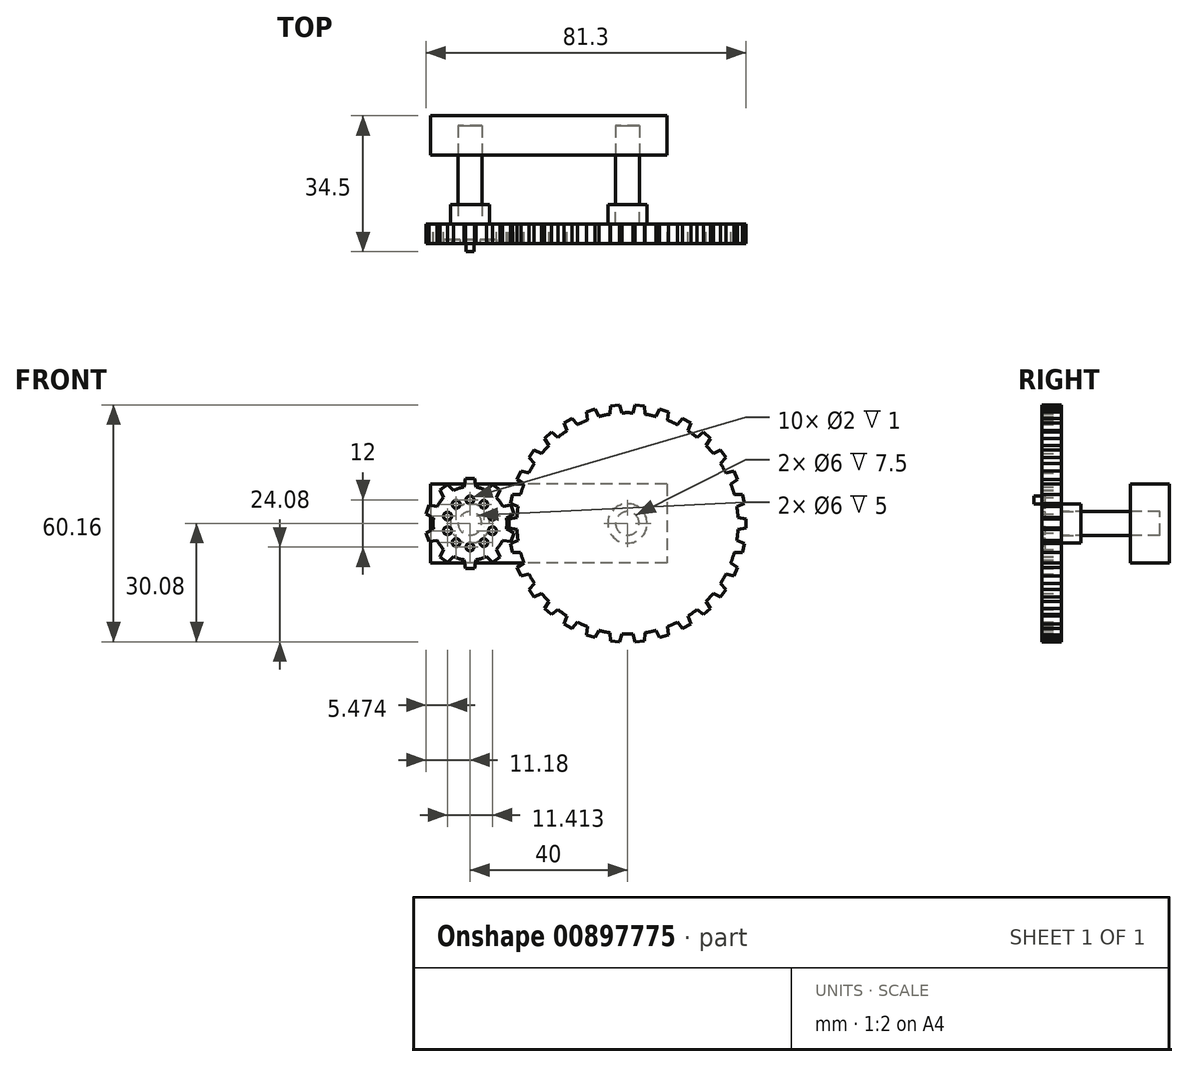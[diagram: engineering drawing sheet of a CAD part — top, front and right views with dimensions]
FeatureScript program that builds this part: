
annotation { "Feature Type Name" : "Feature", "Feature Type Description" : "" }
export const myFeature = defineFeature(function(context is Context, id is Id, definition is map)
    precondition{}
    {
        {
            var Q0;
            Q0=qCreatedBy(makeId("Front.planeOp"),FACE);
            var sketch = newSketch(context, id + "F0", { "sketchPlane" : qUnion([Q0])});
            skCircle(sketch, "E0", {"center": v(0, 0) * mm, "radius": 3 * mm});
            skCircle(sketch, "E1", {"center": v(0, 0) * mm, "radius": 5 * mm});
            skCircle(sketch, "E2", {"center": v(40, 0) * mm, "radius": 3 * mm});
            skCircle(sketch, "E3", {"center": v(40, 0) * mm, "radius": 5 * mm});
            skSolve(sketch);
        }
        {
            var Q0;
            Q0 = qSketchRegion(id + "F0", true);
            extrude(context, id + "F1", {"entities" : qUnion([Q0]), "endBound" : BoundingType.SYMMETRIC, "depth" : 5 * mm, "offsetDistance" : 25 * mm});
        }
        {
            var Q0;
            Q0=makeQuery(id+"F1.opExtrude","CAP_FACE",FACE,{"disambiguationData":[OSD([sQuery(id+"F0.wireOp",EDGE,"E0"),sQuery(id+"F0.wireOp",EDGE,"E1")])],"isStart":false});
            var sketch = newSketch(context, id + "F2", { "sketchPlane" : qUnion([Q0])});
            skCircle(sketch, "E4", {"center": v(0, 0) * mm, "radius": 9.38 * mm});
            skLineSegment(sketch, "E5", {"start": v(0, 11.38) * mm, "end": v(1.18, 11.38) * mm});
            skLineSegment(sketch, "E6", {"start": v(1.18, 11.38) * mm, "end": v(1.55, 9.25) * mm});
            skLineSegment(sketch, "E7.MirrorCS", {"start": v(0, 11.38) * mm, "end": v(-1.18, 11.38) * mm});
            skLineSegment(sketch, "E8.MirrorCS", {"start": v(-1.18, 11.38) * mm, "end": v(-1.55, 9.25) * mm});
            skLineSegment(sketch, "E9.1.0", {"start": v(-7.64, 8.51) * mm, "end": v(-6.7, 6.57) * mm});
            skLineSegment(sketch, "E9.1.1", {"start": v(-6.69, 9.2) * mm, "end": v(-7.64, 8.51) * mm});
            skLineSegment(sketch, "E9.1.2", {"start": v(-6.69, 9.2) * mm, "end": v(-5.73, 9.9) * mm});
            skLineSegment(sketch, "E9.1.3", {"start": v(-5.73, 9.9) * mm, "end": v(-4.18, 8.4) * mm});
            skLineSegment(sketch, "E9.2.0", {"start": v(-11.18, 2.4) * mm, "end": v(-9.27, 1.38) * mm});
            skLineSegment(sketch, "E9.2.1", {"start": v(-10.82, 3.52) * mm, "end": v(-11.18, 2.4) * mm});
            skLineSegment(sketch, "E9.2.2", {"start": v(-10.82, 3.52) * mm, "end": v(-10.45, 4.64) * mm});
            skLineSegment(sketch, "E9.2.3", {"start": v(-10.45, 4.64) * mm, "end": v(-8.31, 4.33) * mm});
            skLineSegment(sketch, "E10.2.3.0", {"start": v(-10.45, -4.64) * mm, "end": v(-8.31, -4.33) * mm});
            skLineSegment(sketch, "E10.3.3.0", {"start": v(-10.82, -3.52) * mm, "end": v(-10.45, -4.64) * mm});
            skLineSegment(sketch, "E10.6.3.0", {"start": v(-10.82, -3.52) * mm, "end": v(-11.18, -2.4) * mm});
            skLineSegment(sketch, "E10.9.3.0", {"start": v(-11.18, -2.4) * mm, "end": v(-9.27, -1.38) * mm});
            skLineSegment(sketch, "E10.2.4.0", {"start": v(-5.73, -9.9) * mm, "end": v(-4.18, -8.4) * mm});
            skLineSegment(sketch, "E10.3.4.0", {"start": v(-6.69, -9.2) * mm, "end": v(-5.73, -9.9) * mm});
            skLineSegment(sketch, "E10.6.4.0", {"start": v(-6.69, -9.2) * mm, "end": v(-7.64, -8.51) * mm});
            skLineSegment(sketch, "E10.9.4.0", {"start": v(-7.64, -8.51) * mm, "end": v(-6.7, -6.57) * mm});
            skLineSegment(sketch, "E10.2.5.0", {"start": v(1.18, -11.38) * mm, "end": v(1.55, -9.25) * mm});
            skLineSegment(sketch, "E10.3.5.0", {"start": v(0, -11.38) * mm, "end": v(1.18, -11.38) * mm});
            skLineSegment(sketch, "E10.6.5.0", {"start": v(0, -11.38) * mm, "end": v(-1.18, -11.38) * mm});
            skLineSegment(sketch, "E10.9.5.0", {"start": v(-1.18, -11.38) * mm, "end": v(-1.55, -9.25) * mm});
            skLineSegment(sketch, "E10.2.6.0", {"start": v(7.64, -8.51) * mm, "end": v(6.7, -6.57) * mm});
            skLineSegment(sketch, "E10.3.6.0", {"start": v(6.69, -9.2) * mm, "end": v(7.64, -8.51) * mm});
            skLineSegment(sketch, "E10.6.6.0", {"start": v(6.69, -9.2) * mm, "end": v(5.73, -9.9) * mm});
            skLineSegment(sketch, "E10.9.6.0", {"start": v(5.73, -9.9) * mm, "end": v(4.18, -8.4) * mm});
            skLineSegment(sketch, "E10.2.7.0", {"start": v(11.18, -2.4) * mm, "end": v(9.27, -1.38) * mm});
            skLineSegment(sketch, "E10.3.7.0", {"start": v(10.82, -3.52) * mm, "end": v(11.18, -2.4) * mm});
            skLineSegment(sketch, "E10.6.7.0", {"start": v(10.82, -3.52) * mm, "end": v(10.45, -4.64) * mm});
            skLineSegment(sketch, "E10.9.7.0", {"start": v(10.45, -4.64) * mm, "end": v(8.31, -4.33) * mm});
            skLineSegment(sketch, "E10.2.8.0", {"start": v(10.45, 4.64) * mm, "end": v(8.31, 4.33) * mm});
            skLineSegment(sketch, "E10.3.8.0", {"start": v(10.82, 3.52) * mm, "end": v(10.45, 4.64) * mm});
            skLineSegment(sketch, "E10.6.8.0", {"start": v(10.82, 3.52) * mm, "end": v(11.18, 2.4) * mm});
            skLineSegment(sketch, "E10.9.8.0", {"start": v(11.18, 2.4) * mm, "end": v(9.27, 1.38) * mm});
            skLineSegment(sketch, "E10.2.9.0", {"start": v(5.73, 9.9) * mm, "end": v(4.18, 8.4) * mm});
            skLineSegment(sketch, "E10.3.9.0", {"start": v(6.69, 9.2) * mm, "end": v(5.73, 9.9) * mm});
            skLineSegment(sketch, "E10.6.9.0", {"start": v(6.69, 9.2) * mm, "end": v(7.64, 8.51) * mm});
            skLineSegment(sketch, "E10.9.9.0", {"start": v(7.64, 8.51) * mm, "end": v(6.7, 6.57) * mm});
            skSolve(sketch);
        }
        {
            var Q0;
            Q0 = qSketchRegion(id + "F2", true);
            extrude(context, id + "F3", {"entities" : qUnion([Q0]), "operationType" : NewBodyOperationType.ADD, "depth" : 5 * mm, "offsetDistance" : 25 * mm});
        }
        {
            var Q0;
            Q0=makeQuery(id+"F1.opExtrude","CAP_FACE",FACE,{"disambiguationData":[OSD([sQuery(id+"F0.wireOp",EDGE,"E2"),sQuery(id+"F0.wireOp",EDGE,"E3")])],"isStart":false});
            var sketch = newSketch(context, id + "F4", { "sketchPlane" : qUnion([Q0])});
            skCircle(sketch, "E11", {"center": v(40, 0) * mm, "radius": 28.13 * mm});
            skLineSegment(sketch, "E12", {"start": v(9.88, 0) * mm, "end": v(9.88, 1.18) * mm});
            skLineSegment(sketch, "E13", {"start": v(9.88, 1.18) * mm, "end": v(11.92, 1.54) * mm});
            skLineSegment(sketch, "E14.MirrorCS", {"start": v(9.88, 0) * mm, "end": v(9.88, -1.18) * mm});
            skLineSegment(sketch, "E15.MirrorCS", {"start": v(9.88, -1.18) * mm, "end": v(11.92, -1.54) * mm});
            skLineSegment(sketch, "E16.1.0", {"start": v(10.53, -6.26) * mm, "end": v(10.29, -5.11) * mm});
            skLineSegment(sketch, "E16.1.1", {"start": v(10.29, -5.11) * mm, "end": v(12.21, -4.33) * mm});
            skLineSegment(sketch, "E16.1.2", {"start": v(10.53, -6.26) * mm, "end": v(10.78, -7.42) * mm});
            skLineSegment(sketch, "E16.1.3", {"start": v(10.78, -7.42) * mm, "end": v(12.85, -7.34) * mm});
            skLineSegment(sketch, "E16.2.0", {"start": v(12.48, -12.25) * mm, "end": v(12, -11.18) * mm});
            skLineSegment(sketch, "E16.2.1", {"start": v(12, -11.18) * mm, "end": v(13.72, -10.02) * mm});
            skLineSegment(sketch, "E16.2.2", {"start": v(12.48, -12.25) * mm, "end": v(12.96, -13.33) * mm});
            skLineSegment(sketch, "E16.2.3", {"start": v(12.96, -13.33) * mm, "end": v(14.97, -12.83) * mm});
            skLineSegment(sketch, "E17.1.3.0", {"start": v(15.63, -17.7) * mm, "end": v(14.94, -16.75) * mm});
            skLineSegment(sketch, "E17.3.3.0", {"start": v(14.94, -16.75) * mm, "end": v(16.38, -15.26) * mm});
            skLineSegment(sketch, "E17.6.3.0", {"start": v(15.63, -17.7) * mm, "end": v(16.32, -18.66) * mm});
            skLineSegment(sketch, "E17.9.3.0", {"start": v(16.32, -18.66) * mm, "end": v(18.18, -17.75) * mm});
            skLineSegment(sketch, "E17.1.4.0", {"start": v(19.84, -22.39) * mm, "end": v(18.97, -21.6) * mm});
            skLineSegment(sketch, "E17.3.4.0", {"start": v(18.97, -21.6) * mm, "end": v(20.07, -19.84) * mm});
            skLineSegment(sketch, "E17.6.4.0", {"start": v(19.84, -22.39) * mm, "end": v(20.72, -23.18) * mm});
            skLineSegment(sketch, "E17.9.4.0", {"start": v(20.72, -23.18) * mm, "end": v(22.35, -21.9) * mm});
            skLineSegment(sketch, "E17.1.5.0", {"start": v(24.94, -26.09) * mm, "end": v(23.92, -25.5) * mm});
            skLineSegment(sketch, "E17.3.5.0", {"start": v(23.92, -25.5) * mm, "end": v(24.63, -23.55) * mm});
            skLineSegment(sketch, "E17.6.5.0", {"start": v(24.94, -26.09) * mm, "end": v(25.96, -26.68) * mm});
            skLineSegment(sketch, "E17.9.5.0", {"start": v(25.96, -26.68) * mm, "end": v(27.3, -25.09) * mm});
            skLineSegment(sketch, "E17.1.6.0", {"start": v(30.7, -28.65) * mm, "end": v(29.57, -28.29) * mm});
            skLineSegment(sketch, "E17.3.6.0", {"start": v(29.57, -28.29) * mm, "end": v(29.86, -26.23) * mm});
            skLineSegment(sketch, "E17.6.6.0", {"start": v(30.7, -28.65) * mm, "end": v(31.81, -29.01) * mm});
            skLineSegment(sketch, "E17.9.6.0", {"start": v(31.81, -29.01) * mm, "end": v(32.78, -27.18) * mm});
            skLineSegment(sketch, "E17.1.7.0", {"start": v(36.85, -29.96) * mm, "end": v(35.68, -29.84) * mm});
            skLineSegment(sketch, "E17.3.7.0", {"start": v(35.68, -29.84) * mm, "end": v(35.53, -27.77) * mm});
            skLineSegment(sketch, "E17.6.7.0", {"start": v(36.85, -29.96) * mm, "end": v(38.02, -30.08) * mm});
            skLineSegment(sketch, "E17.9.7.0", {"start": v(38.02, -30.08) * mm, "end": v(38.6, -28.09) * mm});
            skLineSegment(sketch, "E17.1.8.0", {"start": v(43.15, -29.96) * mm, "end": v(41.98, -30.08) * mm});
            skLineSegment(sketch, "E17.3.8.0", {"start": v(41.98, -30.08) * mm, "end": v(41.4, -28.09) * mm});
            skLineSegment(sketch, "E17.6.8.0", {"start": v(43.15, -29.96) * mm, "end": v(44.32, -29.84) * mm});
            skLineSegment(sketch, "E17.9.8.0", {"start": v(44.32, -29.84) * mm, "end": v(44.47, -27.77) * mm});
            skLineSegment(sketch, "E17.1.9.0", {"start": v(49.3, -28.65) * mm, "end": v(48.19, -29.01) * mm});
            skLineSegment(sketch, "E17.3.9.0", {"start": v(48.19, -29.01) * mm, "end": v(47.22, -27.18) * mm});
            skLineSegment(sketch, "E17.6.9.0", {"start": v(49.3, -28.65) * mm, "end": v(50.43, -28.29) * mm});
            skLineSegment(sketch, "E17.9.9.0", {"start": v(50.43, -28.29) * mm, "end": v(50.14, -26.23) * mm});
            skLineSegment(sketch, "E17.1.10.0", {"start": v(55.06, -26.09) * mm, "end": v(54.04, -26.68) * mm});
            skLineSegment(sketch, "E17.3.10.0", {"start": v(54.04, -26.68) * mm, "end": v(52.7, -25.09) * mm});
            skLineSegment(sketch, "E17.6.10.0", {"start": v(55.06, -26.09) * mm, "end": v(56.08, -25.5) * mm});
            skLineSegment(sketch, "E17.9.10.0", {"start": v(56.08, -25.5) * mm, "end": v(55.37, -23.55) * mm});
            skLineSegment(sketch, "E17.1.11.0", {"start": v(60.16, -22.39) * mm, "end": v(59.28, -23.18) * mm});
            skLineSegment(sketch, "E17.3.11.0", {"start": v(59.28, -23.18) * mm, "end": v(57.65, -21.9) * mm});
            skLineSegment(sketch, "E17.6.11.0", {"start": v(60.16, -22.39) * mm, "end": v(61.03, -21.6) * mm});
            skLineSegment(sketch, "E17.9.11.0", {"start": v(61.03, -21.6) * mm, "end": v(59.93, -19.84) * mm});
            skLineSegment(sketch, "E17.1.12.0", {"start": v(64.37, -17.7) * mm, "end": v(63.68, -18.66) * mm});
            skLineSegment(sketch, "E17.3.12.0", {"start": v(63.68, -18.66) * mm, "end": v(61.82, -17.75) * mm});
            skLineSegment(sketch, "E17.6.12.0", {"start": v(64.37, -17.7) * mm, "end": v(65.06, -16.75) * mm});
            skLineSegment(sketch, "E17.9.12.0", {"start": v(65.06, -16.75) * mm, "end": v(63.62, -15.26) * mm});
            skLineSegment(sketch, "E17.1.13.0", {"start": v(67.52, -12.25) * mm, "end": v(67.04, -13.33) * mm});
            skLineSegment(sketch, "E17.3.13.0", {"start": v(67.04, -13.33) * mm, "end": v(65.03, -12.83) * mm});
            skLineSegment(sketch, "E17.6.13.0", {"start": v(67.52, -12.25) * mm, "end": v(68, -11.18) * mm});
            skLineSegment(sketch, "E17.9.13.0", {"start": v(68, -11.18) * mm, "end": v(66.28, -10.02) * mm});
            skLineSegment(sketch, "E17.1.14.0", {"start": v(69.47, -6.26) * mm, "end": v(69.22, -7.42) * mm});
            skLineSegment(sketch, "E17.3.14.0", {"start": v(69.22, -7.42) * mm, "end": v(67.15, -7.34) * mm});
            skLineSegment(sketch, "E17.6.14.0", {"start": v(69.47, -6.26) * mm, "end": v(69.71, -5.11) * mm});
            skLineSegment(sketch, "E17.9.14.0", {"start": v(69.71, -5.11) * mm, "end": v(67.79, -4.33) * mm});
            skLineSegment(sketch, "E17.1.15.0", {"start": v(70.12, 0) * mm, "end": v(70.12, -1.18) * mm});
            skLineSegment(sketch, "E17.3.15.0", {"start": v(70.13, -1.18) * mm, "end": v(68.08, -1.54) * mm});
            skLineSegment(sketch, "E17.6.15.0", {"start": v(70.12, 0) * mm, "end": v(70.12, 1.18) * mm});
            skLineSegment(sketch, "E17.9.15.0", {"start": v(70.13, 1.18) * mm, "end": v(68.08, 1.54) * mm});
            skLineSegment(sketch, "E17.1.16.0", {"start": v(69.47, 6.26) * mm, "end": v(69.71, 5.11) * mm});
            skLineSegment(sketch, "E17.3.16.0", {"start": v(69.71, 5.11) * mm, "end": v(67.79, 4.33) * mm});
            skLineSegment(sketch, "E17.6.16.0", {"start": v(69.47, 6.26) * mm, "end": v(69.22, 7.42) * mm});
            skLineSegment(sketch, "E17.9.16.0", {"start": v(69.22, 7.42) * mm, "end": v(67.15, 7.34) * mm});
            skLineSegment(sketch, "E17.1.17.0", {"start": v(67.52, 12.25) * mm, "end": v(68, 11.18) * mm});
            skLineSegment(sketch, "E17.3.17.0", {"start": v(68, 11.18) * mm, "end": v(66.28, 10.02) * mm});
            skLineSegment(sketch, "E17.6.17.0", {"start": v(67.52, 12.25) * mm, "end": v(67.04, 13.33) * mm});
            skLineSegment(sketch, "E17.9.17.0", {"start": v(67.04, 13.33) * mm, "end": v(65.03, 12.83) * mm});
            skLineSegment(sketch, "E17.1.18.0", {"start": v(64.37, 17.7) * mm, "end": v(65.06, 16.75) * mm});
            skLineSegment(sketch, "E17.3.18.0", {"start": v(65.06, 16.75) * mm, "end": v(63.62, 15.26) * mm});
            skLineSegment(sketch, "E17.6.18.0", {"start": v(64.37, 17.7) * mm, "end": v(63.68, 18.66) * mm});
            skLineSegment(sketch, "E17.9.18.0", {"start": v(63.68, 18.66) * mm, "end": v(61.82, 17.75) * mm});
            skLineSegment(sketch, "E17.1.19.0", {"start": v(60.16, 22.39) * mm, "end": v(61.03, 21.6) * mm});
            skLineSegment(sketch, "E17.3.19.0", {"start": v(61.03, 21.6) * mm, "end": v(59.93, 19.84) * mm});
            skLineSegment(sketch, "E17.6.19.0", {"start": v(60.16, 22.39) * mm, "end": v(59.28, 23.18) * mm});
            skLineSegment(sketch, "E17.9.19.0", {"start": v(59.28, 23.18) * mm, "end": v(57.65, 21.9) * mm});
            skLineSegment(sketch, "E17.1.20.0", {"start": v(55.06, 26.09) * mm, "end": v(56.08, 25.5) * mm});
            skLineSegment(sketch, "E17.3.20.0", {"start": v(56.08, 25.5) * mm, "end": v(55.37, 23.55) * mm});
            skLineSegment(sketch, "E17.6.20.0", {"start": v(55.06, 26.09) * mm, "end": v(54.04, 26.68) * mm});
            skLineSegment(sketch, "E17.9.20.0", {"start": v(54.04, 26.68) * mm, "end": v(52.7, 25.09) * mm});
            skLineSegment(sketch, "E17.1.21.0", {"start": v(49.3, 28.65) * mm, "end": v(50.43, 28.29) * mm});
            skLineSegment(sketch, "E17.3.21.0", {"start": v(50.43, 28.29) * mm, "end": v(50.14, 26.23) * mm});
            skLineSegment(sketch, "E17.6.21.0", {"start": v(49.3, 28.65) * mm, "end": v(48.19, 29.01) * mm});
            skLineSegment(sketch, "E17.9.21.0", {"start": v(48.19, 29.01) * mm, "end": v(47.22, 27.18) * mm});
            skLineSegment(sketch, "E17.1.22.0", {"start": v(43.15, 29.96) * mm, "end": v(44.32, 29.84) * mm});
            skLineSegment(sketch, "E17.3.22.0", {"start": v(44.32, 29.84) * mm, "end": v(44.47, 27.77) * mm});
            skLineSegment(sketch, "E17.6.22.0", {"start": v(43.15, 29.96) * mm, "end": v(41.98, 30.08) * mm});
            skLineSegment(sketch, "E17.9.22.0", {"start": v(41.98, 30.08) * mm, "end": v(41.4, 28.09) * mm});
            skLineSegment(sketch, "E17.1.23.0", {"start": v(36.85, 29.96) * mm, "end": v(38.02, 30.08) * mm});
            skLineSegment(sketch, "E17.3.23.0", {"start": v(38.02, 30.08) * mm, "end": v(38.6, 28.09) * mm});
            skLineSegment(sketch, "E17.6.23.0", {"start": v(36.85, 29.96) * mm, "end": v(35.68, 29.84) * mm});
            skLineSegment(sketch, "E17.9.23.0", {"start": v(35.68, 29.84) * mm, "end": v(35.53, 27.77) * mm});
            skLineSegment(sketch, "E17.1.24.0", {"start": v(30.7, 28.65) * mm, "end": v(31.81, 29.01) * mm});
            skLineSegment(sketch, "E17.3.24.0", {"start": v(31.81, 29.01) * mm, "end": v(32.78, 27.18) * mm});
            skLineSegment(sketch, "E17.6.24.0", {"start": v(30.7, 28.65) * mm, "end": v(29.57, 28.29) * mm});
            skLineSegment(sketch, "E17.9.24.0", {"start": v(29.57, 28.29) * mm, "end": v(29.86, 26.23) * mm});
            skLineSegment(sketch, "E17.1.25.0", {"start": v(24.94, 26.09) * mm, "end": v(25.96, 26.68) * mm});
            skLineSegment(sketch, "E17.3.25.0", {"start": v(25.96, 26.68) * mm, "end": v(27.3, 25.09) * mm});
            skLineSegment(sketch, "E17.6.25.0", {"start": v(24.94, 26.09) * mm, "end": v(23.92, 25.5) * mm});
            skLineSegment(sketch, "E17.9.25.0", {"start": v(23.92, 25.5) * mm, "end": v(24.63, 23.55) * mm});
            skLineSegment(sketch, "E17.1.26.0", {"start": v(19.84, 22.39) * mm, "end": v(20.72, 23.18) * mm});
            skLineSegment(sketch, "E17.3.26.0", {"start": v(20.72, 23.18) * mm, "end": v(22.35, 21.9) * mm});
            skLineSegment(sketch, "E17.6.26.0", {"start": v(19.84, 22.39) * mm, "end": v(18.97, 21.6) * mm});
            skLineSegment(sketch, "E17.9.26.0", {"start": v(18.97, 21.6) * mm, "end": v(20.07, 19.84) * mm});
            skLineSegment(sketch, "E17.1.27.0", {"start": v(15.63, 17.7) * mm, "end": v(16.32, 18.66) * mm});
            skLineSegment(sketch, "E17.3.27.0", {"start": v(16.32, 18.66) * mm, "end": v(18.18, 17.75) * mm});
            skLineSegment(sketch, "E17.6.27.0", {"start": v(15.63, 17.7) * mm, "end": v(14.94, 16.75) * mm});
            skLineSegment(sketch, "E17.9.27.0", {"start": v(14.94, 16.75) * mm, "end": v(16.38, 15.26) * mm});
            skLineSegment(sketch, "E17.1.28.0", {"start": v(12.48, 12.25) * mm, "end": v(12.96, 13.33) * mm});
            skLineSegment(sketch, "E17.3.28.0", {"start": v(12.96, 13.33) * mm, "end": v(14.97, 12.83) * mm});
            skLineSegment(sketch, "E17.6.28.0", {"start": v(12.48, 12.25) * mm, "end": v(12, 11.18) * mm});
            skLineSegment(sketch, "E17.9.28.0", {"start": v(12, 11.18) * mm, "end": v(13.72, 10.02) * mm});
            skLineSegment(sketch, "E17.1.29.0", {"start": v(10.53, 6.26) * mm, "end": v(10.78, 7.42) * mm});
            skLineSegment(sketch, "E17.3.29.0", {"start": v(10.78, 7.42) * mm, "end": v(12.85, 7.34) * mm});
            skLineSegment(sketch, "E17.6.29.0", {"start": v(10.53, 6.26) * mm, "end": v(10.29, 5.11) * mm});
            skLineSegment(sketch, "E17.9.29.0", {"start": v(10.29, 5.11) * mm, "end": v(12.21, 4.33) * mm});
            skSolve(sketch);
        }
        {
            var Q0;
            Q0 = qSketchRegion(id + "F4", true);
            extrude(context, id + "F5", {"entities" : qUnion([Q0]), "operationType" : NewBodyOperationType.ADD, "depth" : 5 * mm, "offsetDistance" : 25 * mm});
        }
        {
            var Q0;
            Q0=makeQuery(id+"F3.opExtrude","CAP_FACE",FACE,{"disambiguationData":[OSD([sQuery(id+"F2.wireOp",EDGE,"E4"),sQuery(id+"F2.wireOp",EDGE,"E5"),sQuery(id+"F2.wireOp",EDGE,"E6"),sQuery(id+"F2.wireOp",EDGE,"E7.MirrorCS"),sQuery(id+"F2.wireOp",EDGE,"E8.MirrorCS"),sQuery(id+"F2.wireOp",EDGE,"E9.1.0"),sQuery(id+"F2.wireOp",EDGE,"E9.1.1"),sQuery(id+"F2.wireOp",EDGE,"E9.1.2"),sQuery(id+"F2.wireOp",EDGE,"E9.1.3"),sQuery(id+"F2.wireOp",EDGE,"E9.2.0"),sQuery(id+"F2.wireOp",EDGE,"E9.2.1"),sQuery(id+"F2.wireOp",EDGE,"E9.2.2"),sQuery(id+"F2.wireOp",EDGE,"E9.2.3"),sQuery(id+"F2.wireOp",EDGE,"E10.2.3.0"),sQuery(id+"F2.wireOp",EDGE,"E10.3.3.0"),sQuery(id+"F2.wireOp",EDGE,"E10.6.3.0"),sQuery(id+"F2.wireOp",EDGE,"E10.9.3.0"),sQuery(id+"F2.wireOp",EDGE,"E10.2.4.0"),sQuery(id+"F2.wireOp",EDGE,"E10.3.4.0"),sQuery(id+"F2.wireOp",EDGE,"E10.6.4.0"),sQuery(id+"F2.wireOp",EDGE,"E10.9.4.0"),sQuery(id+"F2.wireOp",EDGE,"E10.2.5.0"),sQuery(id+"F2.wireOp",EDGE,"E10.3.5.0"),sQuery(id+"F2.wireOp",EDGE,"E10.6.5.0"),sQuery(id+"F2.wireOp",EDGE,"E10.9.5.0"),sQuery(id+"F2.wireOp",EDGE,"E10.2.6.0"),sQuery(id+"F2.wireOp",EDGE,"E10.3.6.0"),sQuery(id+"F2.wireOp",EDGE,"E10.6.6.0"),sQuery(id+"F2.wireOp",EDGE,"E10.9.6.0"),sQuery(id+"F2.wireOp",EDGE,"E10.2.7.0"),sQuery(id+"F2.wireOp",EDGE,"E10.3.7.0"),sQuery(id+"F2.wireOp",EDGE,"E10.6.7.0"),sQuery(id+"F2.wireOp",EDGE,"E10.9.7.0"),sQuery(id+"F2.wireOp",EDGE,"E10.2.8.0"),sQuery(id+"F2.wireOp",EDGE,"E10.3.8.0"),sQuery(id+"F2.wireOp",EDGE,"E10.6.8.0"),sQuery(id+"F2.wireOp",EDGE,"E10.9.8.0"),sQuery(id+"F2.wireOp",EDGE,"E10.2.9.0"),sQuery(id+"F2.wireOp",EDGE,"E10.3.9.0"),sQuery(id+"F2.wireOp",EDGE,"E10.6.9.0"),sQuery(id+"F2.wireOp",EDGE,"E10.9.9.0")])],"isStart":false});
            var sketch = newSketch(context, id + "F6", { "sketchPlane" : qUnion([Q0])});
            skCircle(sketch, "E18", {"center": v(0, 6) * mm, "radius": 1 * mm});
            skCircle(sketch, "E19.1.0", {"center": v(-3.53, 4.85) * mm, "radius": 1 * mm});
            skCircle(sketch, "E19.2.0", {"center": v(-5.7, 1.85) * mm, "radius": 1 * mm});
            skPoint(sketch, "E19.center", {"position": v(0, 0) * mm});
            skCircle(sketch, "E20.1.3.0", {"center": v(-5.7, -1.85) * mm, "radius": 1 * mm});
            skCircle(sketch, "E20.1.4.0", {"center": v(-3.53, -4.85) * mm, "radius": 1 * mm});
            skCircle(sketch, "E20.1.5.0", {"center": v(0, -6) * mm, "radius": 1 * mm});
            skCircle(sketch, "E20.1.6.0", {"center": v(3.53, -4.85) * mm, "radius": 1 * mm});
            skCircle(sketch, "E20.1.7.0", {"center": v(5.7, -1.85) * mm, "radius": 1 * mm});
            skCircle(sketch, "E20.1.8.0", {"center": v(5.7, 1.85) * mm, "radius": 1 * mm});
            skCircle(sketch, "E20.1.9.0", {"center": v(3.53, 4.85) * mm, "radius": 1 * mm});
            skSolve(sketch);
        }
        {
            var Q0;
            Q0 = qSketchRegion(id + "F6", true);
            extrude(context, id + "F7", {"entities" : qUnion([Q0]), "operationType" : NewBodyOperationType.REMOVE, "oppositeDirection" : true, "depth" : 1 * mm, "offsetDistance" : 25 * mm});
        }
        {
            var Q0;
            Q0=makeQuery(id+"F3.opExtrude","CAP_FACE",FACE,{"disambiguationData":[OSD([sQuery(id+"F2.wireOp",EDGE,"E4"),sQuery(id+"F2.wireOp",EDGE,"E5"),sQuery(id+"F2.wireOp",EDGE,"E6"),sQuery(id+"F2.wireOp",EDGE,"E7.MirrorCS"),sQuery(id+"F2.wireOp",EDGE,"E8.MirrorCS"),sQuery(id+"F2.wireOp",EDGE,"E9.1.0"),sQuery(id+"F2.wireOp",EDGE,"E9.1.1"),sQuery(id+"F2.wireOp",EDGE,"E9.1.2"),sQuery(id+"F2.wireOp",EDGE,"E9.1.3"),sQuery(id+"F2.wireOp",EDGE,"E9.2.0"),sQuery(id+"F2.wireOp",EDGE,"E9.2.1"),sQuery(id+"F2.wireOp",EDGE,"E9.2.2"),sQuery(id+"F2.wireOp",EDGE,"E9.2.3"),sQuery(id+"F2.wireOp",EDGE,"E10.2.3.0"),sQuery(id+"F2.wireOp",EDGE,"E10.3.3.0"),sQuery(id+"F2.wireOp",EDGE,"E10.6.3.0"),sQuery(id+"F2.wireOp",EDGE,"E10.9.3.0"),sQuery(id+"F2.wireOp",EDGE,"E10.2.4.0"),sQuery(id+"F2.wireOp",EDGE,"E10.3.4.0"),sQuery(id+"F2.wireOp",EDGE,"E10.6.4.0"),sQuery(id+"F2.wireOp",EDGE,"E10.9.4.0"),sQuery(id+"F2.wireOp",EDGE,"E10.2.5.0"),sQuery(id+"F2.wireOp",EDGE,"E10.3.5.0"),sQuery(id+"F2.wireOp",EDGE,"E10.6.5.0"),sQuery(id+"F2.wireOp",EDGE,"E10.9.5.0"),sQuery(id+"F2.wireOp",EDGE,"E10.2.6.0"),sQuery(id+"F2.wireOp",EDGE,"E10.3.6.0"),sQuery(id+"F2.wireOp",EDGE,"E10.6.6.0"),sQuery(id+"F2.wireOp",EDGE,"E10.9.6.0"),sQuery(id+"F2.wireOp",EDGE,"E10.2.7.0"),sQuery(id+"F2.wireOp",EDGE,"E10.3.7.0"),sQuery(id+"F2.wireOp",EDGE,"E10.6.7.0"),sQuery(id+"F2.wireOp",EDGE,"E10.9.7.0"),sQuery(id+"F2.wireOp",EDGE,"E10.2.8.0"),sQuery(id+"F2.wireOp",EDGE,"E10.3.8.0"),sQuery(id+"F2.wireOp",EDGE,"E10.6.8.0"),sQuery(id+"F2.wireOp",EDGE,"E10.9.8.0"),sQuery(id+"F2.wireOp",EDGE,"E10.2.9.0"),sQuery(id+"F2.wireOp",EDGE,"E10.3.9.0"),sQuery(id+"F2.wireOp",EDGE,"E10.6.9.0"),sQuery(id+"F2.wireOp",EDGE,"E10.9.9.0")])],"isStart":false});
            var sketch = newSketch(context, id + "F8", { "sketchPlane" : qUnion([Q0])});
            skCircle(sketch, "E21", {"center": v(0, 6) * mm, "radius": 1 * mm});
            skSolve(sketch);
        }
        {
            var Q0;
            Q0 = qSketchRegion(id + "F8", true);
            extrude(context, id + "F9", {"entities" : qUnion([Q0]), "depth" : 2 * mm, "offsetDistance" : 25 * mm});
        }
        {
            var Q0;
            Q0=makeQuery(id+"F5.boolean.opBoolean","SPLIT",FACE,{"disambiguationData":[TD([makeQuery(id+"F1.opExtrude","SWEPT_FACE",FACE,{"disambiguationData":[OSD([sQuery(id+"F0.wireOp",EDGE,"E2")])]})])],"derivedFrom":makeQuery(id+"F5.opExtrude","CAP_FACE",FACE,{"disambiguationData":[OSD([sQuery(id+"F4.wireOp",EDGE,"E11"),sQuery(id+"F4.wireOp",EDGE,"E12"),sQuery(id+"F4.wireOp",EDGE,"E13"),sQuery(id+"F4.wireOp",EDGE,"E14.MirrorCS"),sQuery(id+"F4.wireOp",EDGE,"E15.MirrorCS"),sQuery(id+"F4.wireOp",EDGE,"E16.1.0"),sQuery(id+"F4.wireOp",EDGE,"E16.1.1"),sQuery(id+"F4.wireOp",EDGE,"E16.1.2"),sQuery(id+"F4.wireOp",EDGE,"E16.1.3"),sQuery(id+"F4.wireOp",EDGE,"E16.2.0"),sQuery(id+"F4.wireOp",EDGE,"E16.2.1"),sQuery(id+"F4.wireOp",EDGE,"E16.2.2"),sQuery(id+"F4.wireOp",EDGE,"E16.2.3"),sQuery(id+"F4.wireOp",EDGE,"E17.1.3.0"),sQuery(id+"F4.wireOp",EDGE,"E17.3.3.0"),sQuery(id+"F4.wireOp",EDGE,"E17.6.3.0"),sQuery(id+"F4.wireOp",EDGE,"E17.9.3.0"),sQuery(id+"F4.wireOp",EDGE,"E17.1.4.0"),sQuery(id+"F4.wireOp",EDGE,"E17.3.4.0"),sQuery(id+"F4.wireOp",EDGE,"E17.6.4.0"),sQuery(id+"F4.wireOp",EDGE,"E17.9.4.0"),sQuery(id+"F4.wireOp",EDGE,"E17.1.5.0"),sQuery(id+"F4.wireOp",EDGE,"E17.3.5.0"),sQuery(id+"F4.wireOp",EDGE,"E17.6.5.0"),sQuery(id+"F4.wireOp",EDGE,"E17.9.5.0"),sQuery(id+"F4.wireOp",EDGE,"E17.1.6.0"),sQuery(id+"F4.wireOp",EDGE,"E17.3.6.0"),sQuery(id+"F4.wireOp",EDGE,"E17.6.6.0"),sQuery(id+"F4.wireOp",EDGE,"E17.9.6.0"),sQuery(id+"F4.wireOp",EDGE,"E17.1.7.0"),sQuery(id+"F4.wireOp",EDGE,"E17.3.7.0"),sQuery(id+"F4.wireOp",EDGE,"E17.6.7.0"),sQuery(id+"F4.wireOp",EDGE,"E17.9.7.0"),sQuery(id+"F4.wireOp",EDGE,"E17.1.8.0"),sQuery(id+"F4.wireOp",EDGE,"E17.3.8.0"),sQuery(id+"F4.wireOp",EDGE,"E17.6.8.0"),sQuery(id+"F4.wireOp",EDGE,"E17.9.8.0"),sQuery(id+"F4.wireOp",EDGE,"E17.1.9.0"),sQuery(id+"F4.wireOp",EDGE,"E17.3.9.0"),sQuery(id+"F4.wireOp",EDGE,"E17.6.9.0"),sQuery(id+"F4.wireOp",EDGE,"E17.9.9.0"),sQuery(id+"F4.wireOp",EDGE,"E17.1.10.0"),sQuery(id+"F4.wireOp",EDGE,"E17.3.10.0"),sQuery(id+"F4.wireOp",EDGE,"E17.6.10.0"),sQuery(id+"F4.wireOp",EDGE,"E17.9.10.0"),sQuery(id+"F4.wireOp",EDGE,"E17.1.11.0"),sQuery(id+"F4.wireOp",EDGE,"E17.3.11.0"),sQuery(id+"F4.wireOp",EDGE,"E17.6.11.0"),sQuery(id+"F4.wireOp",EDGE,"E17.9.11.0"),sQuery(id+"F4.wireOp",EDGE,"E17.1.12.0"),sQuery(id+"F4.wireOp",EDGE,"E17.3.12.0"),sQuery(id+"F4.wireOp",EDGE,"E17.6.12.0"),sQuery(id+"F4.wireOp",EDGE,"E17.9.12.0"),sQuery(id+"F4.wireOp",EDGE,"E17.1.13.0"),sQuery(id+"F4.wireOp",EDGE,"E17.3.13.0"),sQuery(id+"F4.wireOp",EDGE,"E17.6.13.0"),sQuery(id+"F4.wireOp",EDGE,"E17.9.13.0"),sQuery(id+"F4.wireOp",EDGE,"E17.1.14.0"),sQuery(id+"F4.wireOp",EDGE,"E17.3.14.0"),sQuery(id+"F4.wireOp",EDGE,"E17.6.14.0"),sQuery(id+"F4.wireOp",EDGE,"E17.9.14.0"),sQuery(id+"F4.wireOp",EDGE,"E17.1.15.0"),sQuery(id+"F4.wireOp",EDGE,"E17.3.15.0"),sQuery(id+"F4.wireOp",EDGE,"E17.6.15.0"),sQuery(id+"F4.wireOp",EDGE,"E17.9.15.0"),sQuery(id+"F4.wireOp",EDGE,"E17.1.16.0"),sQuery(id+"F4.wireOp",EDGE,"E17.3.16.0"),sQuery(id+"F4.wireOp",EDGE,"E17.6.16.0"),sQuery(id+"F4.wireOp",EDGE,"E17.9.16.0"),sQuery(id+"F4.wireOp",EDGE,"E17.1.17.0"),sQuery(id+"F4.wireOp",EDGE,"E17.3.17.0"),sQuery(id+"F4.wireOp",EDGE,"E17.6.17.0"),sQuery(id+"F4.wireOp",EDGE,"E17.9.17.0"),sQuery(id+"F4.wireOp",EDGE,"E17.1.18.0"),sQuery(id+"F4.wireOp",EDGE,"E17.3.18.0"),sQuery(id+"F4.wireOp",EDGE,"E17.6.18.0"),sQuery(id+"F4.wireOp",EDGE,"E17.9.18.0"),sQuery(id+"F4.wireOp",EDGE,"E17.1.19.0"),sQuery(id+"F4.wireOp",EDGE,"E17.3.19.0"),sQuery(id+"F4.wireOp",EDGE,"E17.6.19.0"),sQuery(id+"F4.wireOp",EDGE,"E17.9.19.0"),sQuery(id+"F4.wireOp",EDGE,"E17.1.20.0"),sQuery(id+"F4.wireOp",EDGE,"E17.3.20.0"),sQuery(id+"F4.wireOp",EDGE,"E17.6.20.0"),sQuery(id+"F4.wireOp",EDGE,"E17.9.20.0"),sQuery(id+"F4.wireOp",EDGE,"E17.1.21.0"),sQuery(id+"F4.wireOp",EDGE,"E17.3.21.0"),sQuery(id+"F4.wireOp",EDGE,"E17.6.21.0"),sQuery(id+"F4.wireOp",EDGE,"E17.9.21.0"),sQuery(id+"F4.wireOp",EDGE,"E17.1.22.0"),sQuery(id+"F4.wireOp",EDGE,"E17.3.22.0"),sQuery(id+"F4.wireOp",EDGE,"E17.6.22.0"),sQuery(id+"F4.wireOp",EDGE,"E17.9.22.0"),sQuery(id+"F4.wireOp",EDGE,"E17.1.23.0"),sQuery(id+"F4.wireOp",EDGE,"E17.3.23.0"),sQuery(id+"F4.wireOp",EDGE,"E17.6.23.0"),sQuery(id+"F4.wireOp",EDGE,"E17.9.23.0"),sQuery(id+"F4.wireOp",EDGE,"E17.1.24.0"),sQuery(id+"F4.wireOp",EDGE,"E17.3.24.0"),sQuery(id+"F4.wireOp",EDGE,"E17.6.24.0"),sQuery(id+"F4.wireOp",EDGE,"E17.9.24.0"),sQuery(id+"F4.wireOp",EDGE,"E17.1.25.0"),sQuery(id+"F4.wireOp",EDGE,"E17.3.25.0"),sQuery(id+"F4.wireOp",EDGE,"E17.6.25.0"),sQuery(id+"F4.wireOp",EDGE,"E17.9.25.0"),sQuery(id+"F4.wireOp",EDGE,"E17.1.26.0"),sQuery(id+"F4.wireOp",EDGE,"E17.3.26.0"),sQuery(id+"F4.wireOp",EDGE,"E17.6.26.0"),sQuery(id+"F4.wireOp",EDGE,"E17.9.26.0"),sQuery(id+"F4.wireOp",EDGE,"E17.1.27.0"),sQuery(id+"F4.wireOp",EDGE,"E17.3.27.0"),sQuery(id+"F4.wireOp",EDGE,"E17.6.27.0"),sQuery(id+"F4.wireOp",EDGE,"E17.9.27.0"),sQuery(id+"F4.wireOp",EDGE,"E17.1.28.0"),sQuery(id+"F4.wireOp",EDGE,"E17.3.28.0"),sQuery(id+"F4.wireOp",EDGE,"E17.6.28.0"),sQuery(id+"F4.wireOp",EDGE,"E17.9.28.0"),sQuery(id+"F4.wireOp",EDGE,"E17.1.29.0"),sQuery(id+"F4.wireOp",EDGE,"E17.3.29.0"),sQuery(id+"F4.wireOp",EDGE,"E17.6.29.0"),sQuery(id+"F4.wireOp",EDGE,"E17.9.29.0")])],"isStart":true})});
            extrude(context, id + "F10", {"entities" : qUnion([Q0]), "depth" : 25 * mm, "offsetDistance" : 25 * mm});
        }
        {
            var Q0;
            Q0=makeQuery(id+"F3.boolean.opBoolean","SPLIT",FACE,{"disambiguationData":[TD([makeQuery(id+"F1.opExtrude","SWEPT_FACE",FACE,{"disambiguationData":[OSD([sQuery(id+"F0.wireOp",EDGE,"E0")])]})])],"derivedFrom":makeQuery(id+"F3.opExtrude","CAP_FACE",FACE,{"disambiguationData":[OSD([sQuery(id+"F2.wireOp",EDGE,"E4"),sQuery(id+"F2.wireOp",EDGE,"E5"),sQuery(id+"F2.wireOp",EDGE,"E6"),sQuery(id+"F2.wireOp",EDGE,"E7.MirrorCS"),sQuery(id+"F2.wireOp",EDGE,"E8.MirrorCS"),sQuery(id+"F2.wireOp",EDGE,"E9.1.0"),sQuery(id+"F2.wireOp",EDGE,"E9.1.1"),sQuery(id+"F2.wireOp",EDGE,"E9.1.2"),sQuery(id+"F2.wireOp",EDGE,"E9.1.3"),sQuery(id+"F2.wireOp",EDGE,"E9.2.0"),sQuery(id+"F2.wireOp",EDGE,"E9.2.1"),sQuery(id+"F2.wireOp",EDGE,"E9.2.2"),sQuery(id+"F2.wireOp",EDGE,"E9.2.3"),sQuery(id+"F2.wireOp",EDGE,"E10.2.3.0"),sQuery(id+"F2.wireOp",EDGE,"E10.3.3.0"),sQuery(id+"F2.wireOp",EDGE,"E10.6.3.0"),sQuery(id+"F2.wireOp",EDGE,"E10.9.3.0"),sQuery(id+"F2.wireOp",EDGE,"E10.2.4.0"),sQuery(id+"F2.wireOp",EDGE,"E10.3.4.0"),sQuery(id+"F2.wireOp",EDGE,"E10.6.4.0"),sQuery(id+"F2.wireOp",EDGE,"E10.9.4.0"),sQuery(id+"F2.wireOp",EDGE,"E10.2.5.0"),sQuery(id+"F2.wireOp",EDGE,"E10.3.5.0"),sQuery(id+"F2.wireOp",EDGE,"E10.6.5.0"),sQuery(id+"F2.wireOp",EDGE,"E10.9.5.0"),sQuery(id+"F2.wireOp",EDGE,"E10.2.6.0"),sQuery(id+"F2.wireOp",EDGE,"E10.3.6.0"),sQuery(id+"F2.wireOp",EDGE,"E10.6.6.0"),sQuery(id+"F2.wireOp",EDGE,"E10.9.6.0"),sQuery(id+"F2.wireOp",EDGE,"E10.2.7.0"),sQuery(id+"F2.wireOp",EDGE,"E10.3.7.0"),sQuery(id+"F2.wireOp",EDGE,"E10.6.7.0"),sQuery(id+"F2.wireOp",EDGE,"E10.9.7.0"),sQuery(id+"F2.wireOp",EDGE,"E10.2.8.0"),sQuery(id+"F2.wireOp",EDGE,"E10.3.8.0"),sQuery(id+"F2.wireOp",EDGE,"E10.6.8.0"),sQuery(id+"F2.wireOp",EDGE,"E10.9.8.0"),sQuery(id+"F2.wireOp",EDGE,"E10.2.9.0"),sQuery(id+"F2.wireOp",EDGE,"E10.3.9.0"),sQuery(id+"F2.wireOp",EDGE,"E10.6.9.0"),sQuery(id+"F2.wireOp",EDGE,"E10.9.9.0")])],"isStart":true})});
            extrude(context, id + "F11", {"entities" : qUnion([Q0]), "depth" : 25 * mm, "offsetDistance" : 25 * mm});
        }
        {
            var Q0;
            Q0=qCreatedBy(makeId("Front.planeOp"),FACE);
            cPlane(context, id + "F12", {"entities" : qUnion([Q0]), "cplaneType" : CPlaneType.OFFSET, "offset" : 25 * mm, "oppositeDirection" : true, "width" : 150 * mm, "height" : 150 * mm});
        }
        {
            var Q0;
            Q0=qCreatedBy(id+"F12.planeOp",FACE);
            var sketch = newSketch(context, id + "F13", { "sketchPlane" : qUnion([Q0])});
            skLineSegment(sketch, "E22.bottom", {"start": v(50, 10) * mm, "end": v(-10, 10) * mm});
            skLineSegment(sketch, "E22.top", {"start": v(50, -10) * mm, "end": v(-10, -10) * mm});
            skLineSegment(sketch, "E22.left", {"start": v(50, 10) * mm, "end": v(50, -10) * mm});
            skLineSegment(sketch, "E22.right", {"start": v(-10, 10) * mm, "end": v(-10, -10) * mm});
            skSolve(sketch);
        }
        {
            var Q0;
            Q0 = qSketchRegion(id + "F13", true);
            extrude(context, id + "F14", {"entities" : qUnion([Q0]), "depth" : 10 * mm, "offsetDistance" : 25 * mm});
        }
        {
            var Q0;
            Q0=makeQuery(id+"F10.opExtrude","SWEPT_BODY",BODY,{"disambiguationData":[OSD([sQuery(id+"F4.wireOp",EDGE,"E11"),sQuery(id+"F4.wireOp",EDGE,"E12"),sQuery(id+"F4.wireOp",EDGE,"E13"),sQuery(id+"F4.wireOp",EDGE,"E14.MirrorCS"),sQuery(id+"F4.wireOp",EDGE,"E15.MirrorCS"),sQuery(id+"F4.wireOp",EDGE,"E16.1.0"),sQuery(id+"F4.wireOp",EDGE,"E16.1.1"),sQuery(id+"F4.wireOp",EDGE,"E16.1.2"),sQuery(id+"F4.wireOp",EDGE,"E16.1.3"),sQuery(id+"F4.wireOp",EDGE,"E16.2.0"),sQuery(id+"F4.wireOp",EDGE,"E16.2.1"),sQuery(id+"F4.wireOp",EDGE,"E16.2.2"),sQuery(id+"F4.wireOp",EDGE,"E16.2.3"),sQuery(id+"F4.wireOp",EDGE,"E17.1.3.0"),sQuery(id+"F4.wireOp",EDGE,"E17.3.3.0"),sQuery(id+"F4.wireOp",EDGE,"E17.6.3.0"),sQuery(id+"F4.wireOp",EDGE,"E17.9.3.0"),sQuery(id+"F4.wireOp",EDGE,"E17.1.4.0"),sQuery(id+"F4.wireOp",EDGE,"E17.3.4.0"),sQuery(id+"F4.wireOp",EDGE,"E17.6.4.0"),sQuery(id+"F4.wireOp",EDGE,"E17.9.4.0"),sQuery(id+"F4.wireOp",EDGE,"E17.1.5.0"),sQuery(id+"F4.wireOp",EDGE,"E17.3.5.0"),sQuery(id+"F4.wireOp",EDGE,"E17.6.5.0"),sQuery(id+"F4.wireOp",EDGE,"E17.9.5.0"),sQuery(id+"F4.wireOp",EDGE,"E17.1.6.0"),sQuery(id+"F4.wireOp",EDGE,"E17.3.6.0"),sQuery(id+"F4.wireOp",EDGE,"E17.6.6.0"),sQuery(id+"F4.wireOp",EDGE,"E17.9.6.0"),sQuery(id+"F4.wireOp",EDGE,"E17.1.7.0"),sQuery(id+"F4.wireOp",EDGE,"E17.3.7.0"),sQuery(id+"F4.wireOp",EDGE,"E17.6.7.0"),sQuery(id+"F4.wireOp",EDGE,"E17.9.7.0"),sQuery(id+"F4.wireOp",EDGE,"E17.1.8.0"),sQuery(id+"F4.wireOp",EDGE,"E17.3.8.0"),sQuery(id+"F4.wireOp",EDGE,"E17.6.8.0"),sQuery(id+"F4.wireOp",EDGE,"E17.9.8.0"),sQuery(id+"F4.wireOp",EDGE,"E17.1.9.0"),sQuery(id+"F4.wireOp",EDGE,"E17.3.9.0"),sQuery(id+"F4.wireOp",EDGE,"E17.6.9.0"),sQuery(id+"F4.wireOp",EDGE,"E17.9.9.0"),sQuery(id+"F4.wireOp",EDGE,"E17.1.10.0"),sQuery(id+"F4.wireOp",EDGE,"E17.3.10.0"),sQuery(id+"F4.wireOp",EDGE,"E17.6.10.0"),sQuery(id+"F4.wireOp",EDGE,"E17.9.10.0"),sQuery(id+"F4.wireOp",EDGE,"E17.1.11.0"),sQuery(id+"F4.wireOp",EDGE,"E17.3.11.0"),sQuery(id+"F4.wireOp",EDGE,"E17.6.11.0"),sQuery(id+"F4.wireOp",EDGE,"E17.9.11.0"),sQuery(id+"F4.wireOp",EDGE,"E17.1.12.0"),sQuery(id+"F4.wireOp",EDGE,"E17.3.12.0"),sQuery(id+"F4.wireOp",EDGE,"E17.6.12.0"),sQuery(id+"F4.wireOp",EDGE,"E17.9.12.0"),sQuery(id+"F4.wireOp",EDGE,"E17.1.13.0"),sQuery(id+"F4.wireOp",EDGE,"E17.3.13.0"),sQuery(id+"F4.wireOp",EDGE,"E17.6.13.0"),sQuery(id+"F4.wireOp",EDGE,"E17.9.13.0"),sQuery(id+"F4.wireOp",EDGE,"E17.1.14.0"),sQuery(id+"F4.wireOp",EDGE,"E17.3.14.0"),sQuery(id+"F4.wireOp",EDGE,"E17.6.14.0"),sQuery(id+"F4.wireOp",EDGE,"E17.9.14.0"),sQuery(id+"F4.wireOp",EDGE,"E17.1.15.0"),sQuery(id+"F4.wireOp",EDGE,"E17.3.15.0"),sQuery(id+"F4.wireOp",EDGE,"E17.6.15.0"),sQuery(id+"F4.wireOp",EDGE,"E17.9.15.0"),sQuery(id+"F4.wireOp",EDGE,"E17.1.16.0"),sQuery(id+"F4.wireOp",EDGE,"E17.3.16.0"),sQuery(id+"F4.wireOp",EDGE,"E17.6.16.0"),sQuery(id+"F4.wireOp",EDGE,"E17.9.16.0"),sQuery(id+"F4.wireOp",EDGE,"E17.1.17.0"),sQuery(id+"F4.wireOp",EDGE,"E17.3.17.0"),sQuery(id+"F4.wireOp",EDGE,"E17.6.17.0"),sQuery(id+"F4.wireOp",EDGE,"E17.9.17.0"),sQuery(id+"F4.wireOp",EDGE,"E17.1.18.0"),sQuery(id+"F4.wireOp",EDGE,"E17.3.18.0"),sQuery(id+"F4.wireOp",EDGE,"E17.6.18.0"),sQuery(id+"F4.wireOp",EDGE,"E17.9.18.0"),sQuery(id+"F4.wireOp",EDGE,"E17.1.19.0"),sQuery(id+"F4.wireOp",EDGE,"E17.3.19.0"),sQuery(id+"F4.wireOp",EDGE,"E17.6.19.0"),sQuery(id+"F4.wireOp",EDGE,"E17.9.19.0"),sQuery(id+"F4.wireOp",EDGE,"E17.1.20.0"),sQuery(id+"F4.wireOp",EDGE,"E17.3.20.0"),sQuery(id+"F4.wireOp",EDGE,"E17.6.20.0"),sQuery(id+"F4.wireOp",EDGE,"E17.9.20.0"),sQuery(id+"F4.wireOp",EDGE,"E17.1.21.0"),sQuery(id+"F4.wireOp",EDGE,"E17.3.21.0"),sQuery(id+"F4.wireOp",EDGE,"E17.6.21.0"),sQuery(id+"F4.wireOp",EDGE,"E17.9.21.0"),sQuery(id+"F4.wireOp",EDGE,"E17.1.22.0"),sQuery(id+"F4.wireOp",EDGE,"E17.3.22.0"),sQuery(id+"F4.wireOp",EDGE,"E17.6.22.0"),sQuery(id+"F4.wireOp",EDGE,"E17.9.22.0"),sQuery(id+"F4.wireOp",EDGE,"E17.1.23.0"),sQuery(id+"F4.wireOp",EDGE,"E17.3.23.0"),sQuery(id+"F4.wireOp",EDGE,"E17.6.23.0"),sQuery(id+"F4.wireOp",EDGE,"E17.9.23.0"),sQuery(id+"F4.wireOp",EDGE,"E17.1.24.0"),sQuery(id+"F4.wireOp",EDGE,"E17.3.24.0"),sQuery(id+"F4.wireOp",EDGE,"E17.6.24.0"),sQuery(id+"F4.wireOp",EDGE,"E17.9.24.0"),sQuery(id+"F4.wireOp",EDGE,"E17.1.25.0"),sQuery(id+"F4.wireOp",EDGE,"E17.3.25.0"),sQuery(id+"F4.wireOp",EDGE,"E17.6.25.0"),sQuery(id+"F4.wireOp",EDGE,"E17.9.25.0"),sQuery(id+"F4.wireOp",EDGE,"E17.1.26.0"),sQuery(id+"F4.wireOp",EDGE,"E17.3.26.0"),sQuery(id+"F4.wireOp",EDGE,"E17.6.26.0"),sQuery(id+"F4.wireOp",EDGE,"E17.9.26.0"),sQuery(id+"F4.wireOp",EDGE,"E17.1.27.0"),sQuery(id+"F4.wireOp",EDGE,"E17.3.27.0"),sQuery(id+"F4.wireOp",EDGE,"E17.6.27.0"),sQuery(id+"F4.wireOp",EDGE,"E17.9.27.0"),sQuery(id+"F4.wireOp",EDGE,"E17.1.28.0"),sQuery(id+"F4.wireOp",EDGE,"E17.3.28.0"),sQuery(id+"F4.wireOp",EDGE,"E17.6.28.0"),sQuery(id+"F4.wireOp",EDGE,"E17.9.28.0"),sQuery(id+"F4.wireOp",EDGE,"E17.1.29.0"),sQuery(id+"F4.wireOp",EDGE,"E17.3.29.0"),sQuery(id+"F4.wireOp",EDGE,"E17.6.29.0"),sQuery(id+"F4.wireOp",EDGE,"E17.9.29.0")])]});
            var Q1;
            Q1=makeQuery(id+"F14.opExtrude","SWEPT_BODY",BODY,{"disambiguationData":[OSD([sQuery(id+"F13.wireOp",EDGE,"E22.bottom"),sQuery(id+"F13.wireOp",EDGE,"E22.top"),sQuery(id+"F13.wireOp",EDGE,"E22.left"),sQuery(id+"F13.wireOp",EDGE,"E22.right")])]});
            booleanBodies(context, id + "F15", {"operationType" : BooleanOperationType.SUBTRACTION, "tools" : qUnion([Q0]), "targets" : qUnion([Q1]), "keepTools" : true});
        }
        {
            var Q0;
            Q0=makeQuery(id+"F11.opExtrude","SWEPT_BODY",BODY,{"disambiguationData":[OSD([sQuery(id+"F2.wireOp",EDGE,"E4"),sQuery(id+"F2.wireOp",EDGE,"E5"),sQuery(id+"F2.wireOp",EDGE,"E6"),sQuery(id+"F2.wireOp",EDGE,"E7.MirrorCS"),sQuery(id+"F2.wireOp",EDGE,"E8.MirrorCS"),sQuery(id+"F2.wireOp",EDGE,"E9.1.0"),sQuery(id+"F2.wireOp",EDGE,"E9.1.1"),sQuery(id+"F2.wireOp",EDGE,"E9.1.2"),sQuery(id+"F2.wireOp",EDGE,"E9.1.3"),sQuery(id+"F2.wireOp",EDGE,"E9.2.0"),sQuery(id+"F2.wireOp",EDGE,"E9.2.1"),sQuery(id+"F2.wireOp",EDGE,"E9.2.2"),sQuery(id+"F2.wireOp",EDGE,"E9.2.3"),sQuery(id+"F2.wireOp",EDGE,"E10.2.3.0"),sQuery(id+"F2.wireOp",EDGE,"E10.3.3.0"),sQuery(id+"F2.wireOp",EDGE,"E10.6.3.0"),sQuery(id+"F2.wireOp",EDGE,"E10.9.3.0"),sQuery(id+"F2.wireOp",EDGE,"E10.2.4.0"),sQuery(id+"F2.wireOp",EDGE,"E10.3.4.0"),sQuery(id+"F2.wireOp",EDGE,"E10.6.4.0"),sQuery(id+"F2.wireOp",EDGE,"E10.9.4.0"),sQuery(id+"F2.wireOp",EDGE,"E10.2.5.0"),sQuery(id+"F2.wireOp",EDGE,"E10.3.5.0"),sQuery(id+"F2.wireOp",EDGE,"E10.6.5.0"),sQuery(id+"F2.wireOp",EDGE,"E10.9.5.0"),sQuery(id+"F2.wireOp",EDGE,"E10.2.6.0"),sQuery(id+"F2.wireOp",EDGE,"E10.3.6.0"),sQuery(id+"F2.wireOp",EDGE,"E10.6.6.0"),sQuery(id+"F2.wireOp",EDGE,"E10.9.6.0"),sQuery(id+"F2.wireOp",EDGE,"E10.2.7.0"),sQuery(id+"F2.wireOp",EDGE,"E10.3.7.0"),sQuery(id+"F2.wireOp",EDGE,"E10.6.7.0"),sQuery(id+"F2.wireOp",EDGE,"E10.9.7.0"),sQuery(id+"F2.wireOp",EDGE,"E10.2.8.0"),sQuery(id+"F2.wireOp",EDGE,"E10.3.8.0"),sQuery(id+"F2.wireOp",EDGE,"E10.6.8.0"),sQuery(id+"F2.wireOp",EDGE,"E10.9.8.0"),sQuery(id+"F2.wireOp",EDGE,"E10.2.9.0"),sQuery(id+"F2.wireOp",EDGE,"E10.3.9.0"),sQuery(id+"F2.wireOp",EDGE,"E10.6.9.0"),sQuery(id+"F2.wireOp",EDGE,"E10.9.9.0")])]});
            var Q1;
            Q1=makeQuery(id+"F14.opExtrude","SWEPT_BODY",BODY,{"disambiguationData":[OSD([sQuery(id+"F13.wireOp",EDGE,"E22.bottom"),sQuery(id+"F13.wireOp",EDGE,"E22.top"),sQuery(id+"F13.wireOp",EDGE,"E22.left"),sQuery(id+"F13.wireOp",EDGE,"E22.right")])]});
            booleanBodies(context, id + "F16", {"operationType" : BooleanOperationType.SUBTRACTION, "tools" : qUnion([Q0]), "targets" : qUnion([Q1]), "keepTools" : true});
        }
    });
